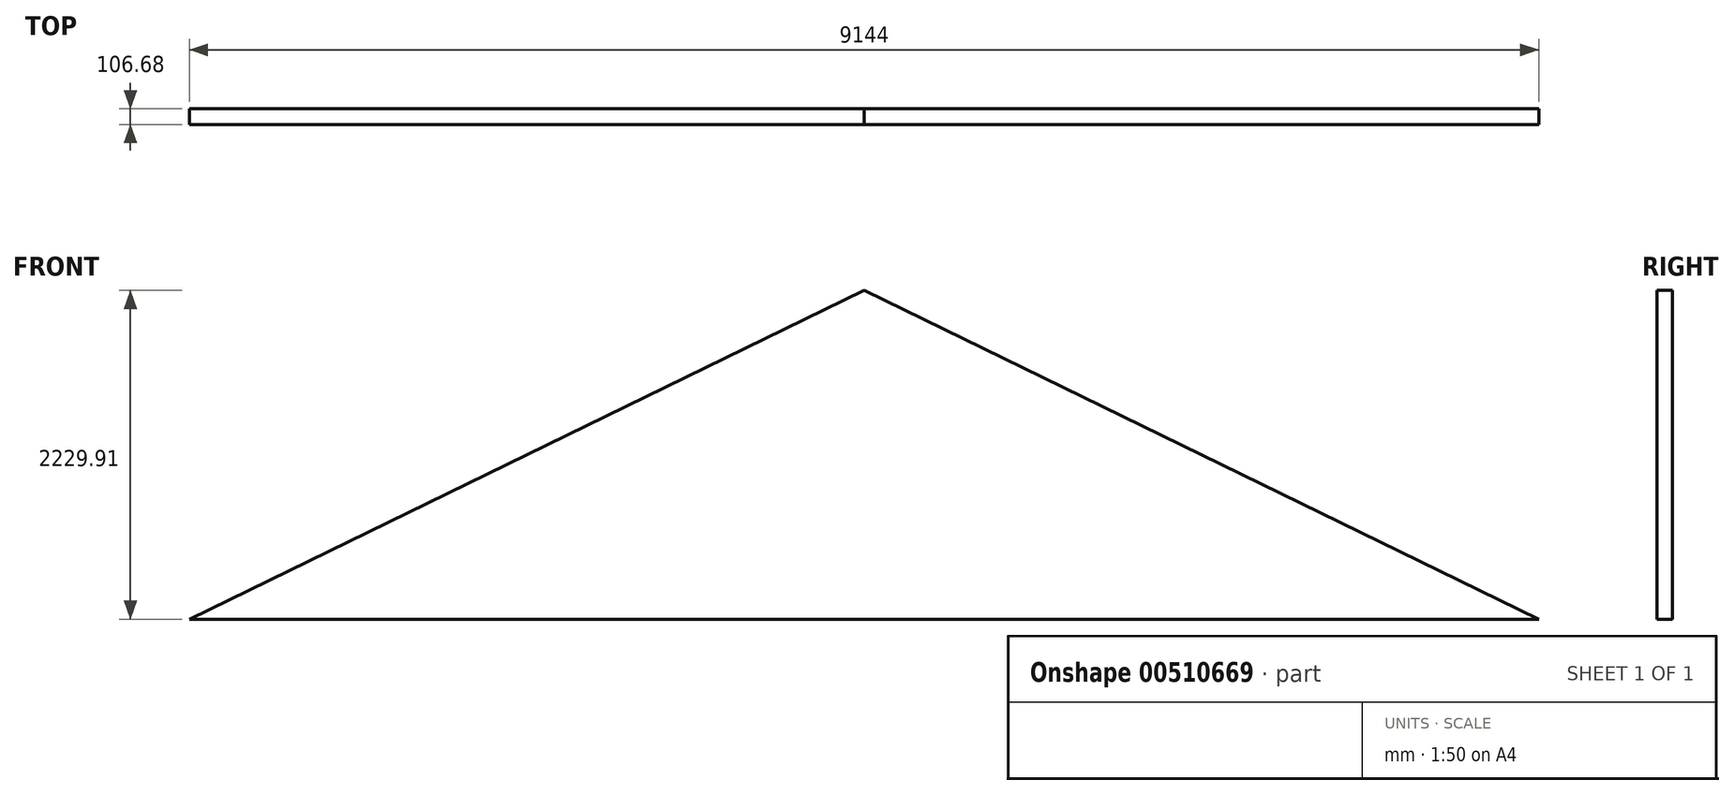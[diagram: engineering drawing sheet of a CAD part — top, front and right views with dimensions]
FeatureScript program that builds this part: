
annotation { "Feature Type Name" : "Feature", "Feature Type Description" : "" }
export const myFeature = defineFeature(function(context is Context, id is Id, definition is map)
    precondition{}
    {
        {
            var Q0;
            Q0=qCreatedBy(makeId("Front.planeOp"),FACE);
            var sketch = newSketch(context, id + "F0", { "sketchPlane" : qUnion([Q0])});
            skLineSegment(sketch, "E0", {"start": v(-4572.95, -1228.92) * mm, "end": v(4571.05, -1228.92) * mm});
            skLineSegment(sketch, "E1", {"start": v(4571.05, -1228.92) * mm, "end": v(-0.95, 1000.99) * mm});
            skLineSegment(sketch, "E2", {"start": v(-0.95, 1000.99) * mm, "end": v(-4572.95, -1228.92) * mm});
            skSolve(sketch);
        }
        {
            var Q0;
            Q0 = qSketchRegion(id + "F0", true);
            extrude(context, id + "F1", {"entities" : qUnion([Q0]), "depth" : 106.68 * mm, "offsetDistance" : 30.48 * mm});
        }
    });
